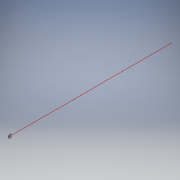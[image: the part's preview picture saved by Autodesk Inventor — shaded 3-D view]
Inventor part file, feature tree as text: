
AUTODESK INVENTOR PART (.ipt)
format: ipt  version: 2016 (Build 200138000, 138)  size: 114,688 bytes
history: native  units: mm
features: sketch x3, extrude x2, fillet x1, hole x1
ambient origin geometry x8: Origin, YZ Plane, XZ Plane, XY Plane, X Axis, Y Axis, Z Axis, Center Point
bodies: Solid1 (feature_tree)
feature tree (7):
  extrude  "Extrusion1"  Depth=1200.0mm TaperAngle=0.0deg
  extrude  "Extrusion2"  Depth=25.0mm
  fillet  "Fillet1"  Radius=25.0mm
  hole  "Hole1"  [1 undecoded]
  sketch  "Sketch1"  dims[d0=2.0mm d1=1200.0mm d2=0.0mm]
  sketch  "Sketch2"  dims[d3=2.0mm d4=25.0mm d5=25.0mm d6=0.0mm]
  sketch  "Sketch3"  dims[d7=10.0mm d8=6.0mm d9=6.0mm d10=6.0mm d11=4.0mm d12=2.0mm d13=90.0deg d14=8.0mm d15=20.594885mm]
note: 1 required parameter value undecoded (feature->parameter linkage not recoverable at this tier; creation-order binding heuristic only, values carry confidence <= 0.55)
